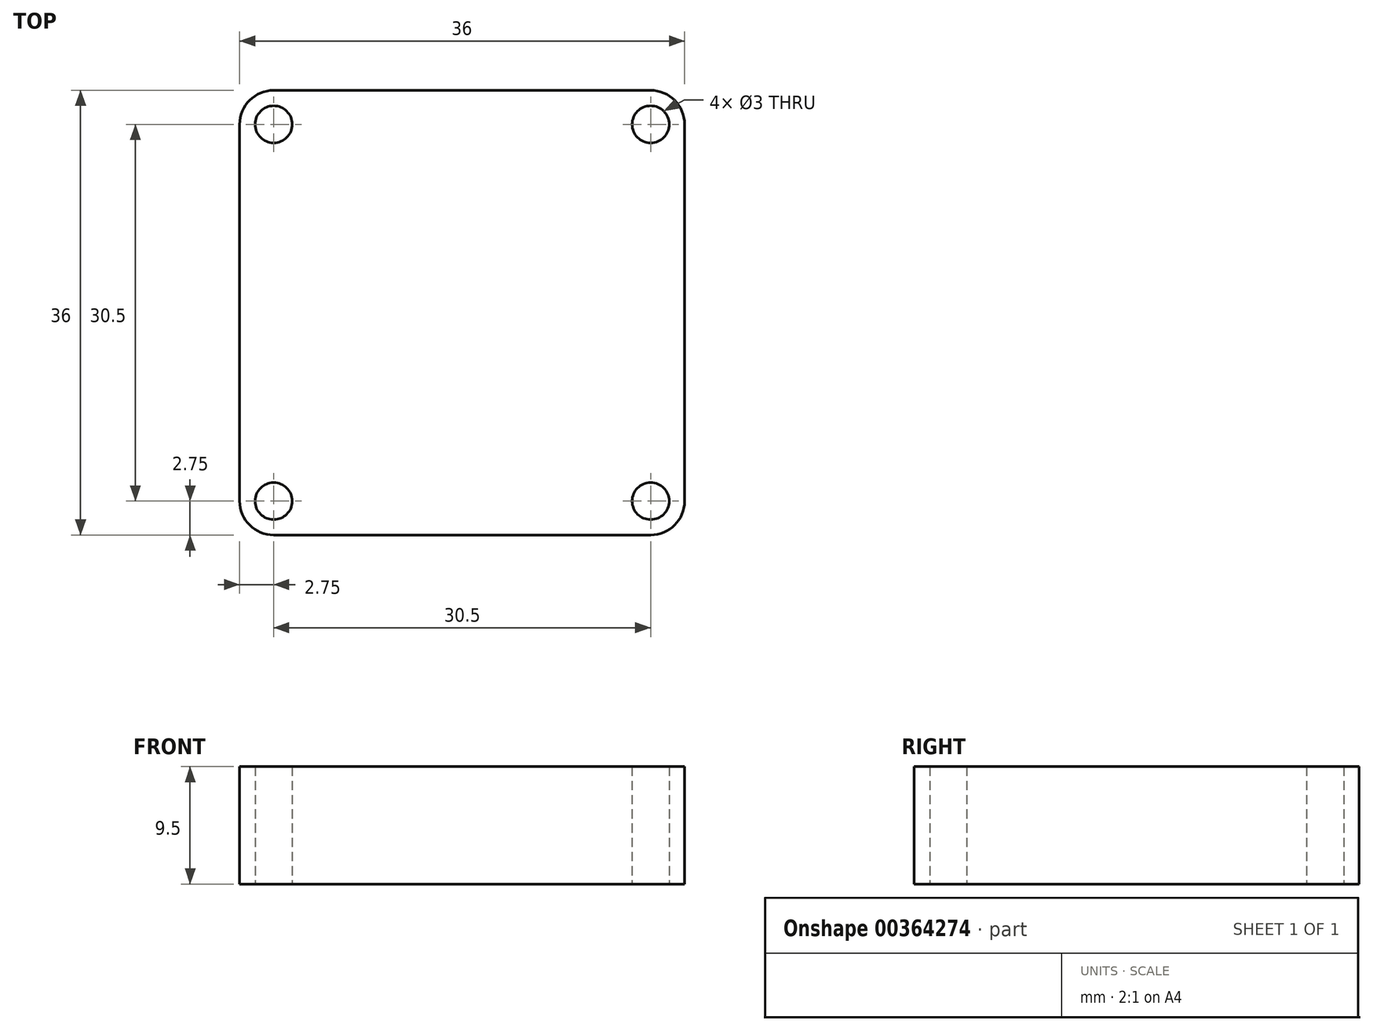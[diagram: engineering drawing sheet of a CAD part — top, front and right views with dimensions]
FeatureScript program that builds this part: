
annotation { "Feature Type Name" : "Feature", "Feature Type Description" : "" }
export const myFeature = defineFeature(function(context is Context, id is Id, definition is map)
    precondition{}
    {
        {
            var Q0;
            Q0=qCreatedBy(makeId("Top.planeOp"),FACE);
            var sketch = newSketch(context, id + "F0", { "sketchPlane" : qUnion([Q0])});
            skLineSegment(sketch, "E0.bottom", {"start": v(-15.25, 18) * mm, "end": v(15.25, 18) * mm});
            skLineSegment(sketch, "E0.top", {"start": v(-15.25, -18) * mm, "end": v(15.25, -18) * mm});
            skLineSegment(sketch, "E0.left", {"start": v(-18, 15.25) * mm, "end": v(-18, -15.25) * mm});
            skLineSegment(sketch, "E0.right", {"start": v(18, 15.25) * mm, "end": v(18, -15.25) * mm});
            skCircle(sketch, "E1", {"center": v(-15.25, 15.25) * mm, "radius": 1.5 * mm});
            skCircle(sketch, "E2.MirrorC", {"center": v(15.25, 15.25) * mm, "radius": 1.5 * mm});
            skCircle(sketch, "E3.MirrorC", {"center": v(-15.25, -15.25) * mm, "radius": 1.5 * mm});
            skCircle(sketch, "E4.MirrorC", {"center": v(15.25, -15.25) * mm, "radius": 1.5 * mm});
            skPoint(sketch, "E5.visualSharp", {"position": v(-18, 18) * mm});
            skArc(sketch, "E5.filletArc", {"start": v(-15.25, 18) * mm, "mid": v(-17.2, 17.2) * mm, "end": v(-18, 15.25) * mm});
            skPoint(sketch, "E6.visualSharp", {"position": v(18, 18) * mm});
            skArc(sketch, "E6.filletArc", {"start": v(18, 15.25) * mm, "mid": v(17.2, 17.2) * mm, "end": v(15.25, 18) * mm});
            skPoint(sketch, "E7.visualSharp", {"position": v(18, -18) * mm});
            skArc(sketch, "E7.filletArc", {"start": v(15.25, -18) * mm, "mid": v(17.2, -17.2) * mm, "end": v(18, -15.25) * mm});
            skPoint(sketch, "E8.visualSharp", {"position": v(-18, -18) * mm});
            skArc(sketch, "E8.filletArc", {"start": v(-18, -15.25) * mm, "mid": v(-17.2, -17.2) * mm, "end": v(-15.25, -18) * mm});
            skSolve(sketch);
        }
        {
            var Q0;
            Q0=makeQuery(id+"F0.imprint","IMPRINT",FACE,{"disambiguationData":[TD([[makeQuery(id+"F0.imprint","IMPRINT",EDGE,{"derivedFrom":sQuery(id+"F0.wireOp",EDGE,"E0.bottom")}),-1.0]])]});
            extrude(context, id + "F1", {"entities" : qUnion([Q0]), "depth" : (1.5 + 8) * mm, "offsetDistance" : 25 * mm});
        }
    });
